# Revit family: Screen-Leg_Mounted-Teknion-JNSEGL-Glass_Elevated-R2018
name_source: partatom
category: Furniture
revit_build: Autodesk Revit 2018 (Build: 20190510_1515(x64)
units: mm (PartAtom-declared; Revit-internal decimal feet)

## family parameters
Always vertical = Yes
Cut with Voids When Loaded = No
OmniClass Number = 23.40.20.00
OmniClass Title = General Furniture and Specialties
Room Calculation Point = No
Shared = Yes
Work Plane-Based = No

## types (5) — shared parameters
Assembly Code = E2020200
Manufacturer = Teknion
Manufacturer Fax = 416.661.4586
Part Number = JNSEGL
Product Documentation Link = https://www.teknion.com
Product Line = Expansion Cityline
Product Page URL = http://www.teknion.com
Series = Expansion Cityline
Sustainability Data = https://www.teknion.com
URL = www.teknion.com
Unit Weight URL = http://www.teknion.com
Warranty = http://www.teknion.com

## per-type parameters (varying)
| type | Description | Double | Left | Left Right Offset | Model | Right | Standard Width |
| Left Configuration - Standard Width | Glass Elevated Screen - Leg Mounted, Left Configuration, 10" Modesty Base Height, Standard Width | No | Yes | 5.331 " | JNSEGLL10__S | No | Yes |
| Right Configuration - Standard Width | Glass Elevated Screen - Leg Mounted, Right Configuration, 10" Modesty Base Height, Standard Width | No | No | 5.331 " | JNSEGLR10__S | Yes | Yes |
| Double- Sided Leg Overlay Configuration | Glass Elevated Screen - Leg Mounted, Double Sided Leg Overlay Configuration, 10" Modesty Base Height, Standard Width | Yes | No | 5.331 " | JNSEGLD10__S | No | Yes |
| Left Configuration - One Side Width Extention | Glass Elevated Screen - Leg Mounted, Left Configuration, 10" Modesty Base Height, One Side Width Extension | No | Yes | 6.081 " | JNSEGLL10__O | No | No |
| Right Configuration - One Side Width Extention | Glass Elevated Screen - Leg Mounted, Right Configuration, 10" Modesty Base Height, One Side Width Extension | No | No | 6.081 " | JNSEGLR10__O | Yes | No |

## geometry (parser evidence)
native form markers: Sweep x2
no freeform markers — native parametric forms only
